# Revit family: Impulsnyy preobrazovatel napryazheniya IPN  AYaKS
name_source: partatom
category: Электрические приборы
units: mm (PartAtom-declared; Revit-internal decimal feet)

## family parameters
Всегда вертикально = Да
Заголовок OmniClass = Electric Power and Lighting
На основе рабочей плоскости = Нет
Номер OmniClass = 23.80.00.00
Общий = Нет
При загрузке вырезать с полостями = Нет
Размер круглого соединителя = Использовать диаметр
Сохранять ориентацию аннотаций = Нет
Тип детали = Нормальный
Точка принадлежности помещению = Нет

## types (2) — shared parameters
ADSK_Единица измерения = шт.
ADSK_Завод-изготовитель = НПП «МАГНИТО-КОНТАКТ»
ADSK_Материал = Пластик белый
ADSK_Примечание = Преобразователь рассчитан на круглосуточный режим работы при температуре окружающей среды от -30 °С до +40 °С и относительной влажности не более 90%.
ADSK_Размер_Высота = 30 мм
ADSK_Размер_Длина = 106 мм
ADSK_Размер_Ширина = 60 мм
URL = https://m-kontakt.ru
Изготовитель = НПП «МАГНИТО-КОНТАКТ»
Кабельные вводы = Да
Метизы = Металл
Мощность потребления = не более 0,8 Вт
Номинальный выходной ток = не более 180 мА
Отметка по умолчанию = 1 мм
Собственный ток потребления = не более 30 мА
Степень защиты, обеспечиваемая оболочкой = IP 65

## per-type parameters (varying)
| type | ADSK_Выходное напряжение | ADSK_Напряжение | ADSK_Обозначение | Допустимые значения напряжения | Описание |
| Импульсный преобразователь напряжения ИПН 24-12 АЯКС | 12 В | 24 В | АТФЕ.469445.001-01ТУ | от 19 до 28 В | Импульсный преобразователь напряжения ИПН 24-12 АЯКС предназначен для преобразования нестабилизированного входного напряжения постоянного тока, находящегося в пределах от 19 до 28 В, в выходное стабилизированное напряжение 12 В постоянного тока. |
| Импульсный преобразователь напряжения ИПН 12-24 АЯКС | 24 В | 12 В | АТФЕ.469445.001ТУ | от 9 до 18 В | Импульсный преобразователь напряжения ИПН 12-24 АЯКС предназначен для преобразования нестабилизированного входного напряжения постоянного тока, находящегося в пределах от 10 до 14 В, в выходное стабилизированное напряжение 24 В постоянного тока. |

note: column(s) folded — value = type name in every type: ADSK_Наименование
